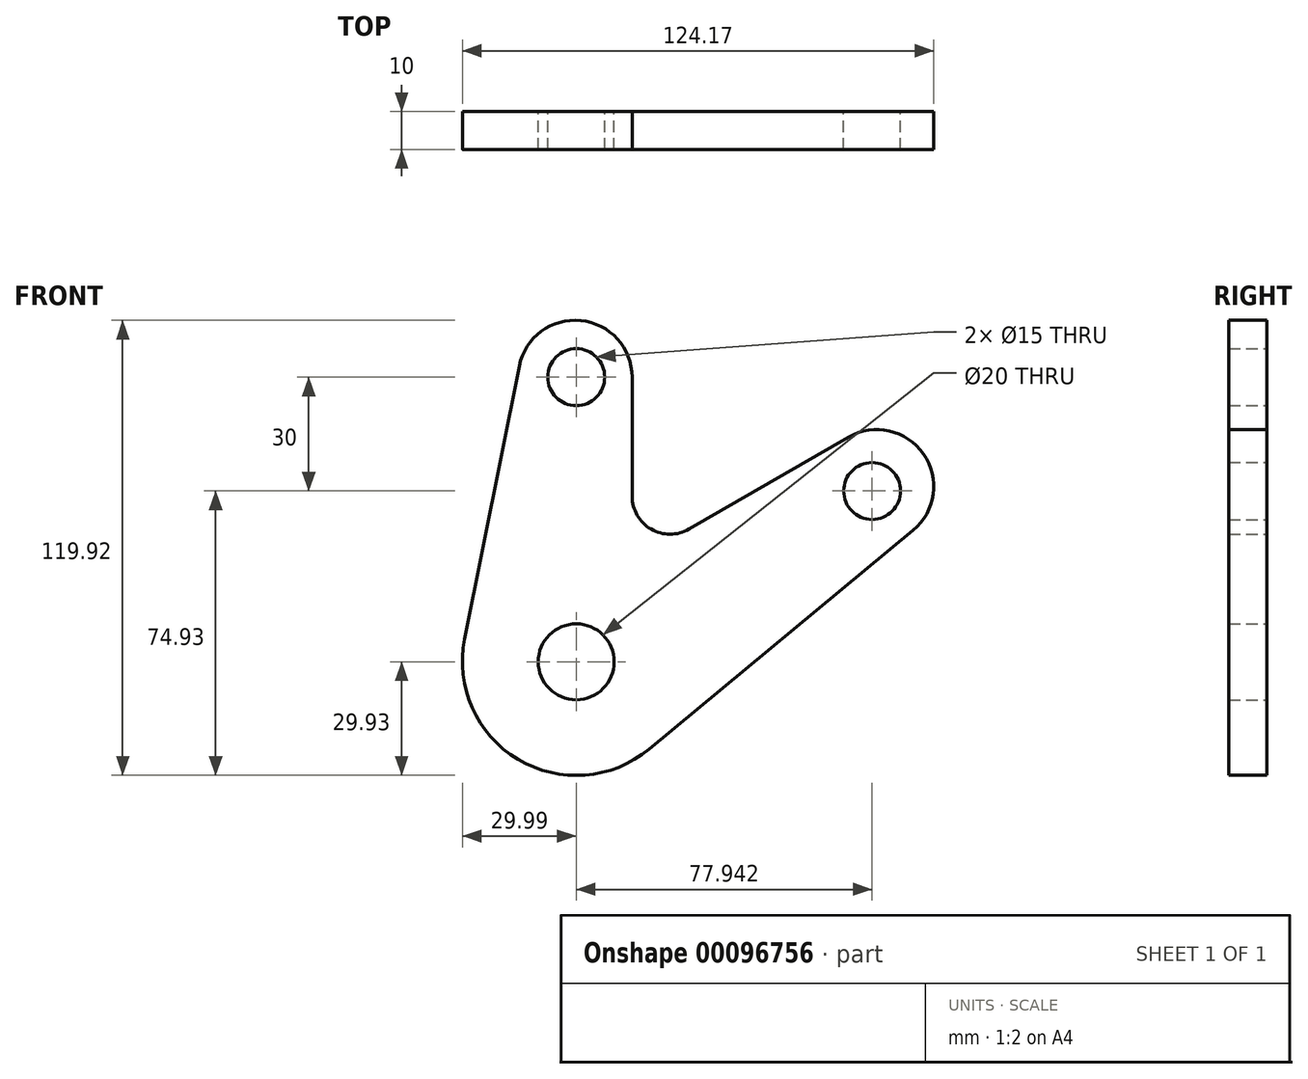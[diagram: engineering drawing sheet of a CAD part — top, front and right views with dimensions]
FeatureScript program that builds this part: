
annotation { "Feature Type Name" : "Feature", "Feature Type Description" : "" }
export const myFeature = defineFeature(function(context is Context, id is Id, definition is map)
    precondition{}
    {
        {
            var Q0;
            Q0=qCreatedBy(makeId("Front.planeOp"),FACE);
            var sketch = newSketch(context, id + "F0", { "sketchPlane" : qUnion([Q0])});
            skCircle(sketch, "E0", {"center": v(0, 0) * mm, "radius": 10 * mm});
            skCircle(sketch, "E1", {"center": v(0, 75) * mm, "radius": 7.5 * mm});
            skLineSegment(sketch, "E2", {"start": v(0, 0) * mm, "end": v(0, 75) * mm, "construction": true});
            skLineSegment(sketch, "E3", {"start": v(0, 0) * mm, "end": v(77.94, 45) * mm, "construction": true});
            skCircle(sketch, "E4", {"center": v(77.94, 45) * mm, "radius": 7.5 * mm});
            skLineSegment(sketch, "E5", {"start": v(-14.99, 77.94) * mm, "end": v(-29.4, 5.96) * mm});
            skLineSegment(sketch, "E6", {"start": v(19.16, -23.03) * mm, "end": v(88.75, 34.65) * mm});
            skArc(sketch, "E7", {"start": v(14.72, 75) * mm, "mid": v(1.2, 89.92) * mm, "end": v(-14.99, 77.94) * mm});
            skArc(sketch, "E8", {"start": v(-29.4, 5.96) * mm, "mid": v(-15.36, -25.7) * mm, "end": v(19.16, -23.03) * mm});
            skArc(sketch, "E9", {"start": v(88.75, 34.65) * mm, "mid": v(91.49, 54.76) * mm, "end": v(71.68, 59.19) * mm});
            skLineSegment(sketch, "E10", {"start": v(14.72, 75) * mm, "end": v(14.72, 43.62) * mm});
            skLineSegment(sketch, "E11", {"start": v(71.68, 59.19) * mm, "end": v(29.72, 34.96) * mm});
            skArc(sketch, "E12", {"start": v(14.72, 43.62) * mm, "mid": v(19.72, 34.96) * mm, "end": v(29.72, 34.96) * mm});
            skSolve(sketch);
        }
        {
            var Q0;
            Q0=makeQuery(id+"F0.imprint","IMPRINT",FACE,{"disambiguationData":[TD([[makeQuery(id+"F0.imprint","IMPRINT",EDGE,{"derivedFrom":sQuery(id+"F0.wireOp",EDGE,"E0")}),-1.0]])]});
            extrude(context, id + "F1", {"entities" : qUnion([Q0]), "depth" : 10 * mm});
        }
    });
